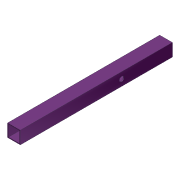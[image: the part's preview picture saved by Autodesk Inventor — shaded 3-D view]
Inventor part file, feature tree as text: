
AUTODESK INVENTOR PART (.ipt)
format: ipt  version: 2012 (Build 160160000, 160)  size: 87,552 bytes
history: native  units: in
note: dims shown in document units (in); Inventor stores cm internally (conversion verified against a paired STEP export)
features: extrude x2, sketch x2, shell x1
ambient origin geometry x8: Origin, YZ Plane, XZ Plane, XY Plane, X Axis, Y Axis, Z Axis, Center Point
bodies: Solid1 (feature_tree)
feature tree (5):
  extrude  "Extrusion1"  Depth=1.0in
  shell  "Shell1"  Thickness=12.0in
  extrude  "Extrusion2"  Depth=0.5in
  sketch  "Sketch1"  dims[d0=1.0in d1=1.0in d2=12.0in d3=0.0in]
  sketch  "Sketch2"  dims[d4=0.0625in d5=0.5in d6=8.0in d7=12.0in d8=0.0in d9=0.375in]
